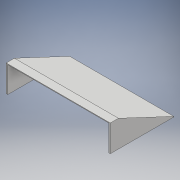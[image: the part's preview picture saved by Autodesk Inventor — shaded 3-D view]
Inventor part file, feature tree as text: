
AUTODESK INVENTOR PART (.ipt)
format: ipt  version: 2018.2 (Build 222227000, 227)  size: 140,800 bytes
history: native  units: mm
features: extrude x5, sketch x5
ambient origin geometry x8: Origin, YZ Plane, XZ Plane, XY Plane, X Axis, Y Axis, Z Axis, Center Point
bodies: Solid1 (feature_tree)
feature tree (10):
  extrude  "Extrusion1"  Depth=160.0mm
  extrude  "Extrusion2"  Depth=2.4mm
  extrude  "Extrusion3"  Depth=155.2mm TaperAngle=0.0deg
  extrude  "Extrusion5"  Depth=2.4mm TaperAngle=0.0deg
  extrude  "Extrusion6"  Depth=2.4mm TaperAngle=0.0deg
  sketch  "Sketch1"  dims[d0=85.0mm d1=160.0mm]
  sketch  "Sketch2"  dims[d2=2.4mm d3=82.6mm]
  sketch  "Sketch3"  dims[d4=155.2mm d5=0.9mm d6=0.0mm]
  sketch  "Sketch5"  dims[d7=40.0mm d8=2.4mm d9=0.0mm]
  sketch  "Sketch6"  dims[d10=2.4mm d11=0.0mm d18=156.0mm d19=0.0mm d20=12.6mm d21=0.0mm]
